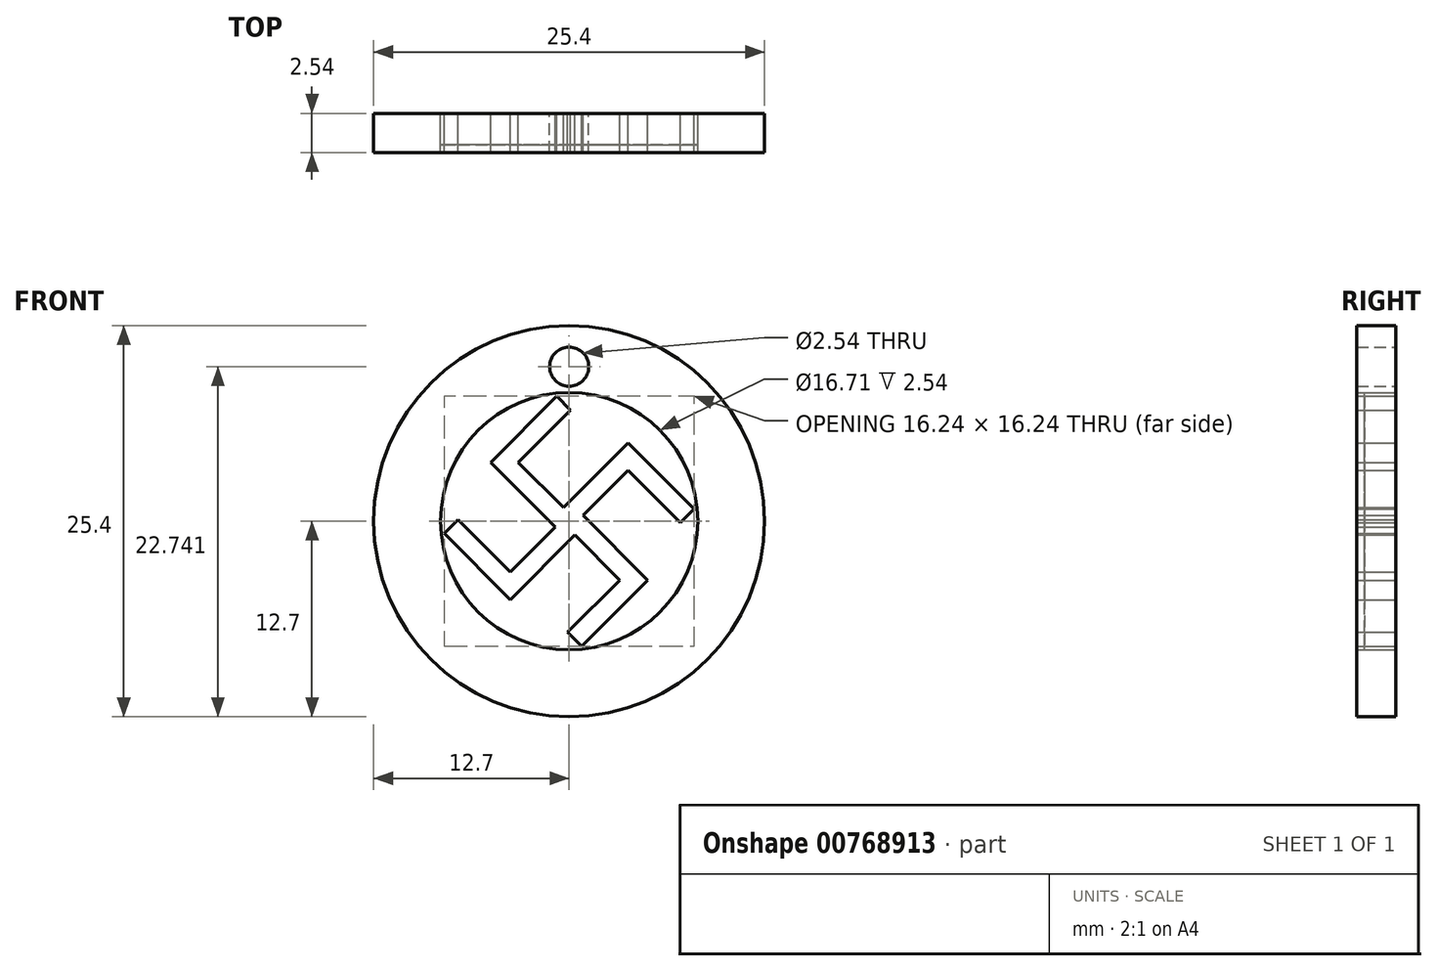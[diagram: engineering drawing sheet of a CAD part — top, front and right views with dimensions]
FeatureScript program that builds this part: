
annotation { "Feature Type Name" : "Feature", "Feature Type Description" : "" }
export const myFeature = defineFeature(function(context is Context, id is Id, definition is map)
    precondition{}
    {
        {
            var Q0;
            Q0=qCreatedBy(makeId("Front.planeOp"),FACE);
            var sketch = newSketch(context, id + "F0", { "sketchPlane" : qUnion([Q0])});
            skCircle(sketch, "E0", {"center": v(0, 0) * mm, "radius": 12.7 * mm});
            skCircle(sketch, "E1", {"center": v(0, 10.04) * mm, "radius": 1.27 * mm});
            skCircle(sketch, "E2", {"center": v(0, 0) * mm, "radius": 8.35 * mm});
            skLineSegment(sketch, "E3", {"start": v(-0.9, -0.37) * mm, "end": v(-5.1, 3.83) * mm});
            skLineSegment(sketch, "E4", {"start": v(-5.1, 3.83) * mm, "end": v(-0.8, 8.12) * mm});
            skLineSegment(sketch, "E5", {"start": v(-0.8, 8.12) * mm, "end": v(0.1, 7.22) * mm});
            skLineSegment(sketch, "E6", {"start": v(0.1, 7.22) * mm, "end": v(-3.3, 3.83) * mm});
            skLineSegment(sketch, "E7", {"start": v(-3.3, 3.83) * mm, "end": v(-0.37, 0.9) * mm});
            skLineSegment(sketch, "E8.1.0", {"start": v(0.37, -0.9) * mm, "end": v(-3.83, -5.1) * mm});
            skLineSegment(sketch, "E8.1.1", {"start": v(-3.83, -3.3) * mm, "end": v(-0.9, -0.37) * mm});
            skLineSegment(sketch, "E8.1.3", {"start": v(-3.83, -5.1) * mm, "end": v(-8.12, -0.8) * mm});
            skLineSegment(sketch, "E8.1.4", {"start": v(-7.22, 0.1) * mm, "end": v(-3.83, -3.3) * mm});
            skLineSegment(sketch, "E8.1.5", {"start": v(-8.12, -0.8) * mm, "end": v(-7.22, 0.1) * mm});
            skLineSegment(sketch, "E8.2.1", {"start": v(3.3, -3.83) * mm, "end": v(0.37, -0.9) * mm});
            skLineSegment(sketch, "E8.2.3", {"start": v(5.1, -3.83) * mm, "end": v(0.8, -8.12) * mm});
            skLineSegment(sketch, "E8.2.4", {"start": v(-0.1, -7.22) * mm, "end": v(3.3, -3.83) * mm});
            skLineSegment(sketch, "E8.2.5", {"start": v(0.8, -8.12) * mm, "end": v(-0.1, -7.22) * mm});
            skLineSegment(sketch, "E8.3.0", {"start": v(-0.37, 0.9) * mm, "end": v(3.83, 5.1) * mm});
            skLineSegment(sketch, "E8.3.1", {"start": v(3.83, 3.3) * mm, "end": v(0.9, 0.37) * mm});
            skLineSegment(sketch, "E8.3.3", {"start": v(3.83, 5.1) * mm, "end": v(8.12, 0.8) * mm});
            skLineSegment(sketch, "E8.3.4", {"start": v(7.22, -0.1) * mm, "end": v(3.83, 3.3) * mm});
            skLineSegment(sketch, "E8.3.5", {"start": v(8.12, 0.8) * mm, "end": v(7.22, -0.1) * mm});
            skPoint(sketch, "E9.orphan", {"position": v(0.6, 0.66) * mm});
            skPoint(sketch, "E10.orphan", {"position": v(0.3, 0.23) * mm});
            skPoint(sketch, "E11.orphan", {"position": v(-0.23, 0.3) * mm});
            skPoint(sketch, "E12.orphan", {"position": v(0.23, -0.3) * mm});
            skPoint(sketch, "E13.orphan", {"position": v(-0.66, 0.6) * mm});
            skPoint(sketch, "E14.orphan", {"position": v(-0.6, -0.66) * mm});
            skLineSegment(sketch, "E15", {"start": v(5.1, -3.83) * mm, "end": v(0.9, 0.37) * mm});
            skPoint(sketch, "E16.orphan", {"position": v(0.66, -0.6) * mm});
            skSolve(sketch);
        }
        {
            var Q0;
            Q0=makeQuery(id+"F0.imprint","IMPRINT",FACE,{"disambiguationData":[TD([[makeQuery(id+"F0.imprint","IMPRINT",EDGE,{"derivedFrom":sQuery(id+"F0.wireOp",EDGE,"E0")}),1.0]])]});
            var Q1;
            Q1=makeQuery(id+"F0.imprint","IMPRINT",FACE,{"disambiguationData":[TD([[makeQuery(id+"F0.imprint","IMPRINT",EDGE,{"derivedFrom":sQuery(id+"F0.wireOp",EDGE,"E3")}),-1.0]])]});
            extrude(context, id + "F1", {"entities" : qUnion([Q0, Q1]), "depth" : 2.54 * mm, "offsetDistance" : 25.4 * mm});
        }
        {
            var Q0;
            Q0=makeQuery(id+"F0.imprint","IMPRINT",FACE,{"disambiguationData":[TD([[makeQuery(id+"F0.imprint","IMPRINT",EDGE,{"derivedFrom":sQuery(id+"F0.wireOp",EDGE,"E2")}),1.0]])]});
            extrude(context, id + "F2", {"entities" : qUnion([Q0]), "depth" : 2.03 * mm, "offsetDistance" : 25.4 * mm});
        }
    });
